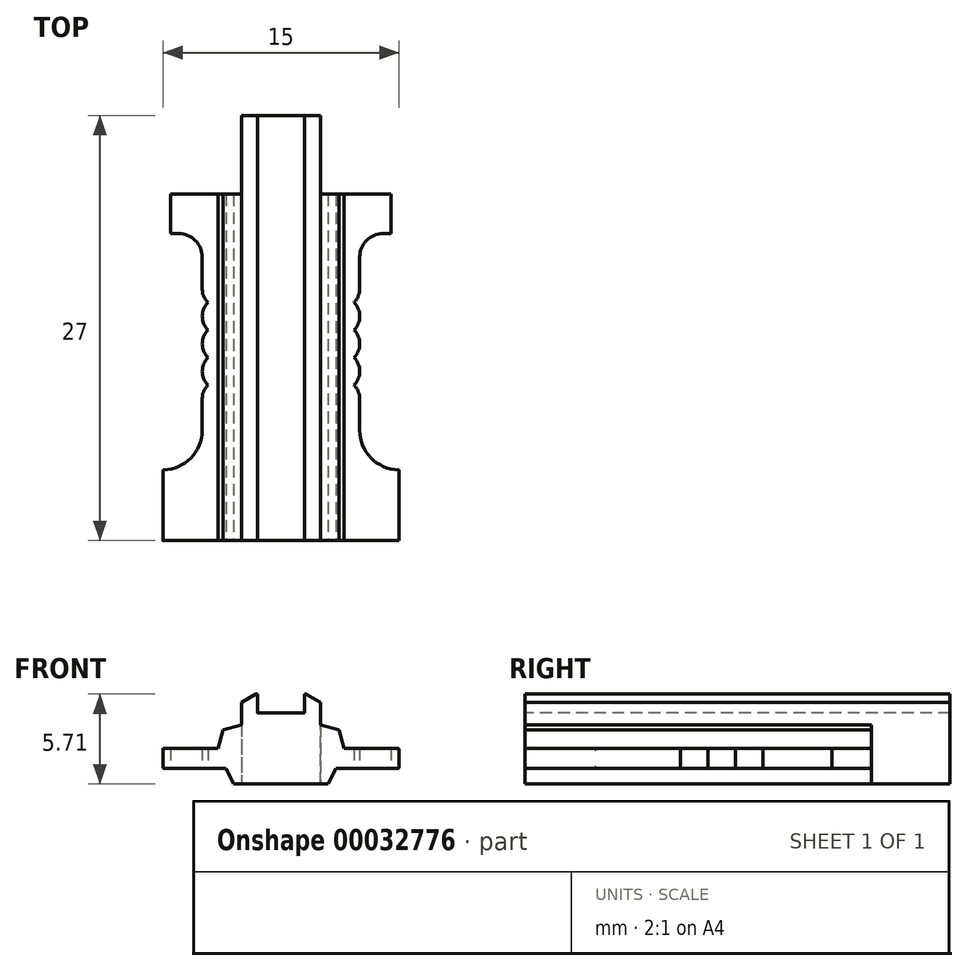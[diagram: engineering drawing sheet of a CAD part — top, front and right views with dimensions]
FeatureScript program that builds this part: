
annotation { "Feature Type Name" : "Feature", "Feature Type Description" : "" }
export const myFeature = defineFeature(function(context is Context, id is Id, definition is map)
    precondition{}
    {
        {
            var Q0;
            Q0=qCreatedBy(makeId("Front.planeOp"),FACE);
            var sketch = newSketch(context, id + "F0", { "sketchPlane" : qUnion([Q0])});
            skLineSegment(sketch, "E0", {"start": v(-7.45, 0) * mm, "end": v(-3.5, 0) * mm});
            skLineSegment(sketch, "E1", {"start": v(-3, -1) * mm, "end": v(3, -1) * mm});
            skLineSegment(sketch, "E2", {"start": v(3, -1) * mm, "end": v(3.5, 0) * mm});
            skLineSegment(sketch, "E3", {"start": v(-3, -1) * mm, "end": v(-3.5, 0) * mm});
            skLineSegment(sketch, "E4", {"start": v(7.5, 0.05) * mm, "end": v(7.5, 1.2) * mm});
            skLineSegment(sketch, "E5", {"start": v(7.45, 1.25) * mm, "end": v(4, 1.25) * mm});
            skLineSegment(sketch, "E6", {"start": v(-7.5, 0.05) * mm, "end": v(-7.5, 1.2) * mm});
            skLineSegment(sketch, "E7", {"start": v(-7.45, 1.25) * mm, "end": v(-4, 1.25) * mm});
            skLineSegment(sketch, "E8.trimOffspring", {"start": v(3.5, 0) * mm, "end": v(7.45, 0) * mm});
            skLineSegment(sketch, "E9", {"start": v(2.5, 2.75) * mm, "end": v(2.5, 4.17) * mm});
            skLineSegment(sketch, "E10", {"start": v(1.5, 4.66) * mm, "end": v(1.5, 3.55) * mm});
            skLineSegment(sketch, "E11", {"start": v(1.45, 3.5) * mm, "end": v(-1.45, 3.5) * mm});
            skLineSegment(sketch, "E12", {"start": v(-1.5, 3.55) * mm, "end": v(-1.5, 4.66) * mm});
            skLineSegment(sketch, "E13", {"start": v(-2.5, 4.17) * mm, "end": v(-2.5, 2.75) * mm});
            skLineSegment(sketch, "E14", {"start": v(4, 1.25) * mm, "end": v(3.68, 2.43) * mm});
            skLineSegment(sketch, "E15", {"start": v(2.5, 2.75) * mm, "end": v(3.68, 2.43) * mm});
            skLineSegment(sketch, "E16", {"start": v(1.57, 4.7) * mm, "end": v(2.5, 4.17) * mm});
            skPoint(sketch, "E17.visualSharp", {"position": v(1.5, 4.75) * mm});
            skArc(sketch, "E17.filletArc", {"start": v(1.58, 4.7) * mm, "mid": v(1.53, 4.7) * mm, "end": v(1.5, 4.66) * mm});
            skPoint(sketch, "E18.visualSharp", {"position": v(1.5, 3.5) * mm});
            skArc(sketch, "E18.filletArc", {"start": v(1.45, 3.5) * mm, "mid": v(1.49, 3.51) * mm, "end": v(1.5, 3.55) * mm});
            skPoint(sketch, "E19.visualSharp", {"position": v(-1.5, 3.5) * mm});
            skArc(sketch, "E19.filletArc", {"start": v(-1.5, 3.55) * mm, "mid": v(-1.49, 3.51) * mm, "end": v(-1.45, 3.5) * mm});
            skLineSegment(sketch, "E20", {"start": v(-1.57, 4.7) * mm, "end": v(-2.5, 4.17) * mm});
            skPoint(sketch, "E21.visualSharp", {"position": v(-1.5, 4.75) * mm});
            skArc(sketch, "E21.filletArc", {"start": v(-1.5, 4.66) * mm, "mid": v(-1.52, 4.7) * mm, "end": v(-1.57, 4.7) * mm});
            skLineSegment(sketch, "E22", {"start": v(-2.5, 2.75) * mm, "end": v(-3.68, 2.43) * mm});
            skLineSegment(sketch, "E23", {"start": v(-4, 1.25) * mm, "end": v(-3.68, 2.43) * mm});
            skPoint(sketch, "E24.visualSharp", {"position": v(7.5, 1.25) * mm});
            skArc(sketch, "E24.filletArc", {"start": v(7.5, 1.2) * mm, "mid": v(7.49, 1.24) * mm, "end": v(7.45, 1.25) * mm});
            skPoint(sketch, "E25.visualSharp", {"position": v(7.5, 0) * mm});
            skArc(sketch, "E25.filletArc", {"start": v(7.45, 0) * mm, "mid": v(7.49, 0.01) * mm, "end": v(7.5, 0.05) * mm});
            skPoint(sketch, "E26.visualSharp", {"position": v(-7.5, 0) * mm});
            skArc(sketch, "E26.filletArc", {"start": v(-7.5, 0.05) * mm, "mid": v(-7.49, 0.01) * mm, "end": v(-7.45, 0) * mm});
            skPoint(sketch, "E27.visualSharp", {"position": v(-7.5, 1.25) * mm});
            skArc(sketch, "E27.filletArc", {"start": v(-7.45, 1.25) * mm, "mid": v(-7.49, 1.24) * mm, "end": v(-7.5, 1.2) * mm});
            skSolve(sketch);
        }
        {
            var Q0;
            Q0=makeQuery(id+"F0.imprint","IMPRINT",FACE,{"disambiguationData":[TD([[makeQuery(id+"F0.imprint","IMPRINT",EDGE,{"derivedFrom":sQuery(id+"F0.wireOp",EDGE,"E0")}),1.0]])]});
            extrude(context, id + "F1", {"entities" : qUnion([Q0]), "oppositeDirection" : true, "depth" : 27 * mm});
        }
        {
            var Q0;
            Q0=qCreatedBy(makeId("Top.planeOp"),FACE);
            var sketch = newSketch(context, id + "F2", { "sketchPlane" : qUnion([Q0])});
            skLineSegment(sketch, "E28", {"start": v(0, 0) * mm, "end": v(7.5, 0) * mm});
            skLineSegment(sketch, "E29", {"start": v(5, 7) * mm, "end": v(5, 9) * mm});
            skLineSegment(sketch, "E30", {"start": v(6.5, 19.5) * mm, "end": v(6.95, 19.5) * mm});
            skLineSegment(sketch, "E31", {"start": v(7, 19.55) * mm, "end": v(7, 22) * mm});
            skArc(sketch, "E32.trimOffspring", {"start": v(5, 7) * mm, "mid": v(5.71, 5.25) * mm, "end": v(7.45, 4.5) * mm});
            skPoint(sketch, "E33.visualSharp", {"position": v(7.5, 4.5) * mm});
            skArc(sketch, "E33.filletArc", {"start": v(7.5, 4.45) * mm, "mid": v(7.49, 4.49) * mm, "end": v(7.45, 4.5) * mm});
            skArc(sketch, "E34", {"start": v(6.5, 19.5) * mm, "mid": v(5.44, 19.06) * mm, "end": v(5, 18) * mm});
            skPoint(sketch, "E35.visualSharp", {"position": v(7, 19.5) * mm});
            skArc(sketch, "E35.filletArc", {"start": v(6.95, 19.5) * mm, "mid": v(6.99, 19.51) * mm, "end": v(7, 19.55) * mm});
            skLineSegment(sketch, "E36", {"start": v(7, 22) * mm, "end": v(2.5, 22) * mm});
            skLineSegment(sketch, "E37", {"start": v(2.5, 22) * mm, "end": v(2.5, 27) * mm});
            skLineSegment(sketch, "E38", {"start": v(2.5, 27) * mm, "end": v(7.5, 27) * mm});
            skLineSegment(sketch, "E39", {"start": v(7.5, 27) * mm, "end": v(7.5, 4.45) * mm});
            skArc(sketch, "E40", {"start": v(4.64, 15.12) * mm, "mid": v(4.9, 15.53) * mm, "end": v(5, 16) * mm});
            skArc(sketch, "E41.1.0.0", {"start": v(4.64, 13.37) * mm, "mid": v(5, 14.25) * mm, "end": v(4.64, 15.12) * mm});
            skLineSegment(sketch, "E41.2.0.0", {"start": v(2.86, 11.62) * mm, "end": v(2.86, 11.62) * mm});
            skArc(sketch, "E41.3.0.0", {"start": v(4.64, 9.87) * mm, "mid": v(5, 10.75) * mm, "end": v(4.64, 11.62) * mm});
            skArc(sketch, "E41.4.0.0", {"start": v(5, 9) * mm, "mid": v(4.9, 9.47) * mm, "end": v(4.64, 9.87) * mm});
            skLineSegment(sketch, "E41.direction1", {"start": v(3.75, 16) * mm, "end": v(3.75, 14.25) * mm, "construction": true});
            skLineSegment(sketch, "E42.trimOffspring", {"start": v(5, 10.75) * mm, "end": v(5, 10.75) * mm});
            skLineSegment(sketch, "E43.trimOffspring", {"start": v(5, 12.5) * mm, "end": v(5, 12.5) * mm});
            skLineSegment(sketch, "E44.trimOffspring", {"start": v(5, 14.25) * mm, "end": v(5, 14.25) * mm});
            skLineSegment(sketch, "E45.trimOffspring", {"start": v(5, 16) * mm, "end": v(5, 18) * mm});
            skArc(sketch, "E46.trimOffspring", {"start": v(4.64, 11.62) * mm, "mid": v(5, 12.5) * mm, "end": v(4.64, 13.37) * mm});
            skArc(sketch, "E47.MirrorCS", {"start": v(-7.5, 4.45) * mm, "mid": v(-7.49, 4.49) * mm, "end": v(-7.45, 4.5) * mm});
            skArc(sketch, "E48.MirrorCS", {"start": v(-6.95, 19.5) * mm, "mid": v(-6.99, 19.51) * mm, "end": v(-7, 19.55) * mm});
            skLineSegment(sketch, "E49.MirrorCS", {"start": v(-6.5, 19.5) * mm, "end": v(-6.95, 19.5) * mm});
            skArc(sketch, "E50.MirrorCS", {"start": v(-4.64, 9.87) * mm, "mid": v(-5, 10.75) * mm, "end": v(-4.64, 11.62) * mm});
            skArc(sketch, "E51.MirrorCS", {"start": v(-4.64, 11.62) * mm, "mid": v(-5, 12.5) * mm, "end": v(-4.64, 13.37) * mm});
            skPoint(sketch, "E52.MirrorP", {"position": v(-7, 19.5) * mm});
            skArc(sketch, "E53.MirrorCS", {"start": v(-4.64, 13.37) * mm, "mid": v(-5, 14.25) * mm, "end": v(-4.64, 15.12) * mm});
            skLineSegment(sketch, "E54.MirrorCS", {"start": v(-7, 22) * mm, "end": v(-2.5, 22) * mm});
            skArc(sketch, "E55.MirrorCS", {"start": v(-5, 7) * mm, "mid": v(-5.71, 5.25) * mm, "end": v(-7.45, 4.5) * mm});
            skLineSegment(sketch, "E56.MirrorCS", {"start": v(-2.5, 22) * mm, "end": v(-2.5, 27) * mm});
            skLineSegment(sketch, "E57.MirrorCS", {"start": v(0, 0) * mm, "end": v(-7.5, 0) * mm});
            skLineSegment(sketch, "E58.MirrorCS", {"start": v(-7, 19.55) * mm, "end": v(-7, 22) * mm});
            skLineSegment(sketch, "E59.MirrorCS", {"start": v(-5, 14.25) * mm, "end": v(-5, 14.25) * mm});
            skLineSegment(sketch, "E60.MirrorCS", {"start": v(-5, 7) * mm, "end": v(-5, 9) * mm});
            skArc(sketch, "E61.MirrorCS", {"start": v(-4.64, 15.12) * mm, "mid": v(-4.9, 15.53) * mm, "end": v(-5, 16) * mm});
            skArc(sketch, "E62.MirrorCS", {"start": v(-5, 9) * mm, "mid": v(-4.9, 9.47) * mm, "end": v(-4.64, 9.87) * mm});
            skLineSegment(sketch, "E63.MirrorCS", {"start": v(-2.86, 11.62) * mm, "end": v(-2.86, 11.62) * mm});
            skLineSegment(sketch, "E64.MirrorCS", {"start": v(-2.5, 27) * mm, "end": v(-7.5, 27) * mm});
            skLineSegment(sketch, "E65.MirrorCS", {"start": v(-7.5, 27) * mm, "end": v(-7.5, 4.45) * mm});
            skLineSegment(sketch, "E66.MirrorCS", {"start": v(-3.75, 16) * mm, "end": v(-3.75, 14.25) * mm});
            skLineSegment(sketch, "E67.MirrorCS", {"start": v(-5, 16) * mm, "end": v(-5, 18) * mm});
            skLineSegment(sketch, "E68.MirrorCS", {"start": v(-5, 12.5) * mm, "end": v(-5, 12.5) * mm});
            skPoint(sketch, "E69.MirrorP", {"position": v(-7.5, 4.5) * mm});
            skLineSegment(sketch, "E70.MirrorCS", {"start": v(-5, 10.75) * mm, "end": v(-5, 10.75) * mm});
            skArc(sketch, "E71.MirrorCS", {"start": v(-6.5, 19.5) * mm, "mid": v(-5.44, 19.06) * mm, "end": v(-5, 18) * mm});
            skSolve(sketch);
        }
        {
            var Q0;
            Q0 = qSketchRegion(id + "F2", true);
            extrude(context, id + "F3", {"entities" : qUnion([Q0]), "operationType" : NewBodyOperationType.REMOVE, "endBound" : BoundingType.SYMMETRIC, "depth" : 10 * mm});
        }
    });
